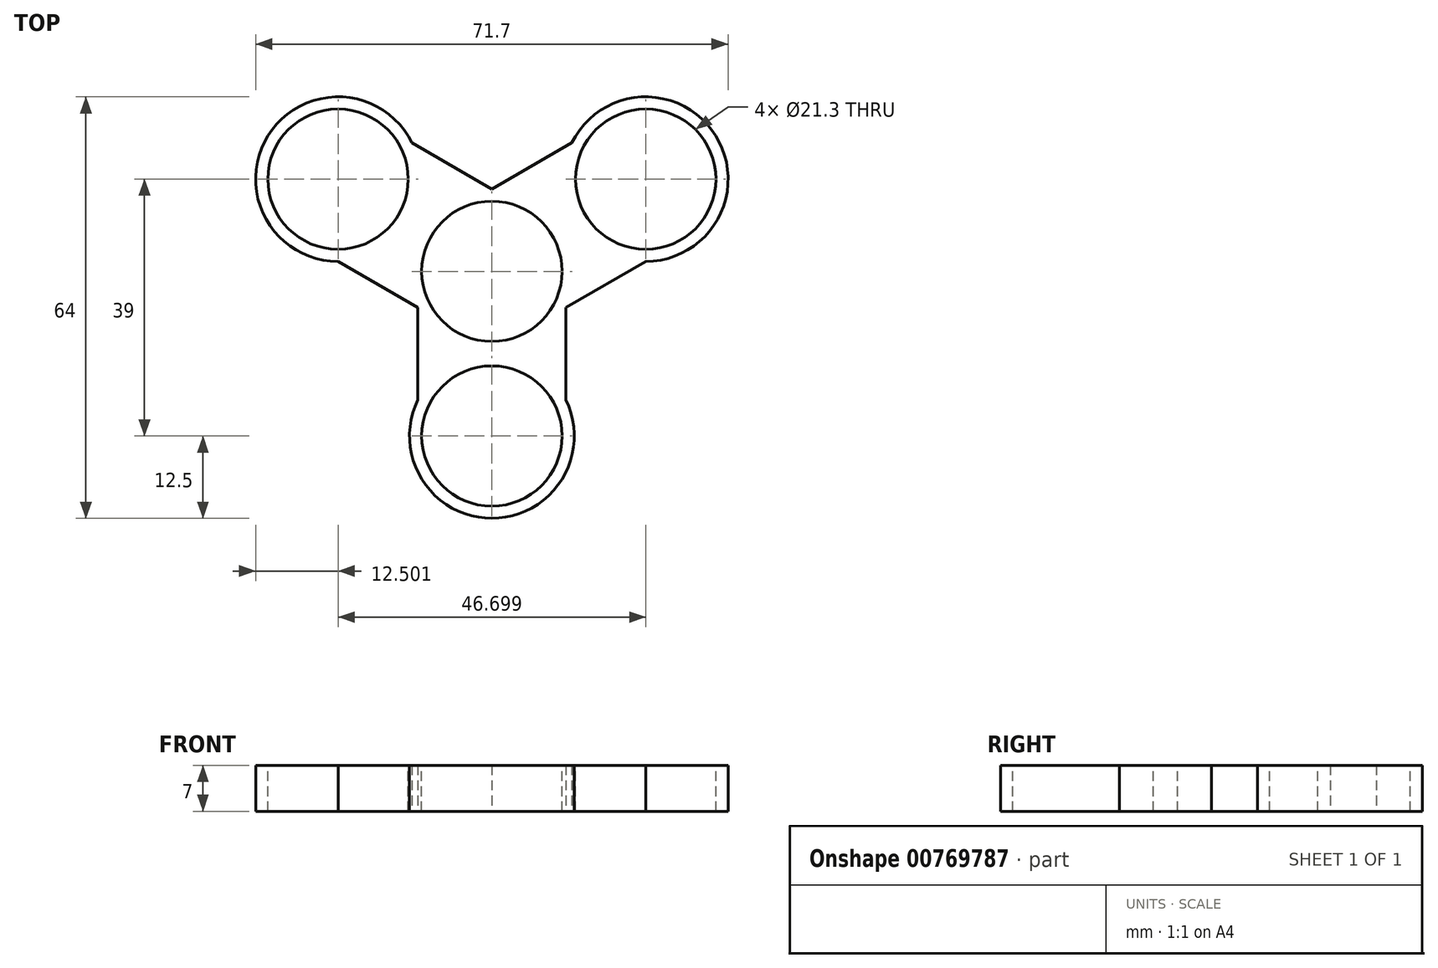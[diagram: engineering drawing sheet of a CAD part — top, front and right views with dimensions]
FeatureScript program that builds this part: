
annotation { "Feature Type Name" : "Feature", "Feature Type Description" : "" }
export const myFeature = defineFeature(function(context is Context, id is Id, definition is map)
    precondition{}
    {
        {
            var Q0;
            Q0=qCreatedBy(makeId("Top.planeOp"),FACE);
            var sketch = newSketch(context, id + "F0", { "sketchPlane" : qUnion([Q0])});
            skCircle(sketch, "E0", {"center": v(0, 0) * mm, "radius": 12.5 * mm});
            skArc(sketch, "E1", {"start": v(-11.22, -19.5) * mm, "mid": v(0, -37.5) * mm, "end": v(11.22, -19.5) * mm});
            skLineSegment(sketch, "E2.left", {"start": v(-11.22, -5.5) * mm, "end": v(-11.22, -19.5) * mm});
            skLineSegment(sketch, "E2.right", {"start": v(11.22, -5.5) * mm, "end": v(11.22, -19.5) * mm});
            skArc(sketch, "E3", {"start": v(-12.12, 19.5) * mm, "mid": v(-33.96, 20.61) * mm, "end": v(-23.35, 1.5) * mm});
            skLineSegment(sketch, "E4.left", {"start": v(0, 12.5) * mm, "end": v(-12.12, 19.5) * mm});
            skLineSegment(sketch, "E4.right", {"start": v(-11.22, -5.5) * mm, "end": v(-23.35, 1.5) * mm});
            skArc(sketch, "E5", {"start": v(23.35, 1.5) * mm, "mid": v(33.96, 20.61) * mm, "end": v(12.12, 19.5) * mm});
            skLineSegment(sketch, "E6.left", {"start": v(11.22, -5.5) * mm, "end": v(23.35, 1.5) * mm});
            skLineSegment(sketch, "E6.right", {"start": v(0, 12.5) * mm, "end": v(12.12, 19.5) * mm});
            skSolve(sketch);
        }
        {
            var Q0;
            Q0 = qSketchRegion(id + "F0", true);
            extrude(context, id + "F1", {"entities" : qUnion([Q0]), "endBound" : BoundingType.SYMMETRIC, "depth" : 7 * mm, "offsetDistance" : 25 * mm});
        }
        {
            var Q0;
            Q0=makeQuery(id+"F1.opExtrude","CAP_FACE",FACE,{"disambiguationData":[OSD([sQuery(id+"F0.wireOp",EDGE,"E1"),sQuery(id+"F0.wireOp",EDGE,"E2.left"),sQuery(id+"F0.wireOp",EDGE,"E2.right"),sQuery(id+"F0.wireOp",EDGE,"E3"),sQuery(id+"F0.wireOp",EDGE,"E4.left"),sQuery(id+"F0.wireOp",EDGE,"E4.right"),sQuery(id+"F0.wireOp",EDGE,"E5"),sQuery(id+"F0.wireOp",EDGE,"E6.left"),sQuery(id+"F0.wireOp",EDGE,"E6.right")])],"isStart":false});
            var sketch = newSketch(context, id + "F2", { "sketchPlane" : qUnion([Q0])});
            skCircle(sketch, "E7", {"center": v(-23.35, 14) * mm, "radius": 10.65 * mm});
            skCircle(sketch, "E8", {"center": v(23.35, 14) * mm, "radius": 10.65 * mm});
            skCircle(sketch, "E9", {"center": v(0, -25) * mm, "radius": 10.65 * mm});
            skCircle(sketch, "E10", {"center": v(0, 0) * mm, "radius": 10.65 * mm});
            skSolve(sketch);
        }
        {
            var Q0;
            Q0=makeQuery(id+"F2.imprint","IMPRINT",FACE,{"disambiguationData":[TD([[makeQuery(id+"F2.imprint","IMPRINT",EDGE,{"derivedFrom":sQuery(id+"F2.wireOp",EDGE,"E7")}),1.0]])]});
            var Q1;
            Q1=makeQuery(id+"F2.imprint","IMPRINT",FACE,{"disambiguationData":[TD([[makeQuery(id+"F2.imprint","IMPRINT",EDGE,{"derivedFrom":sQuery(id+"F2.wireOp",EDGE,"E10")}),1.0]])]});
            var Q2;
            Q2=makeQuery(id+"F2.imprint","IMPRINT",FACE,{"disambiguationData":[TD([[makeQuery(id+"F2.imprint","IMPRINT",EDGE,{"derivedFrom":sQuery(id+"F2.wireOp",EDGE,"E8")}),1.0]])]});
            var Q3;
            Q3=makeQuery(id+"F2.imprint","IMPRINT",FACE,{"disambiguationData":[TD([[makeQuery(id+"F2.imprint","IMPRINT",EDGE,{"derivedFrom":sQuery(id+"F2.wireOp",EDGE,"E9")}),1.0]])]});
            extrude(context, id + "F3", {"entities" : qUnion([Q0, Q1, Q2, Q3]), "operationType" : NewBodyOperationType.REMOVE, "endBound" : BoundingType.SYMMETRIC, "oppositeDirection" : true, "depth" : 14 * mm, "offsetDistance" : 25 * mm});
        }
    });
